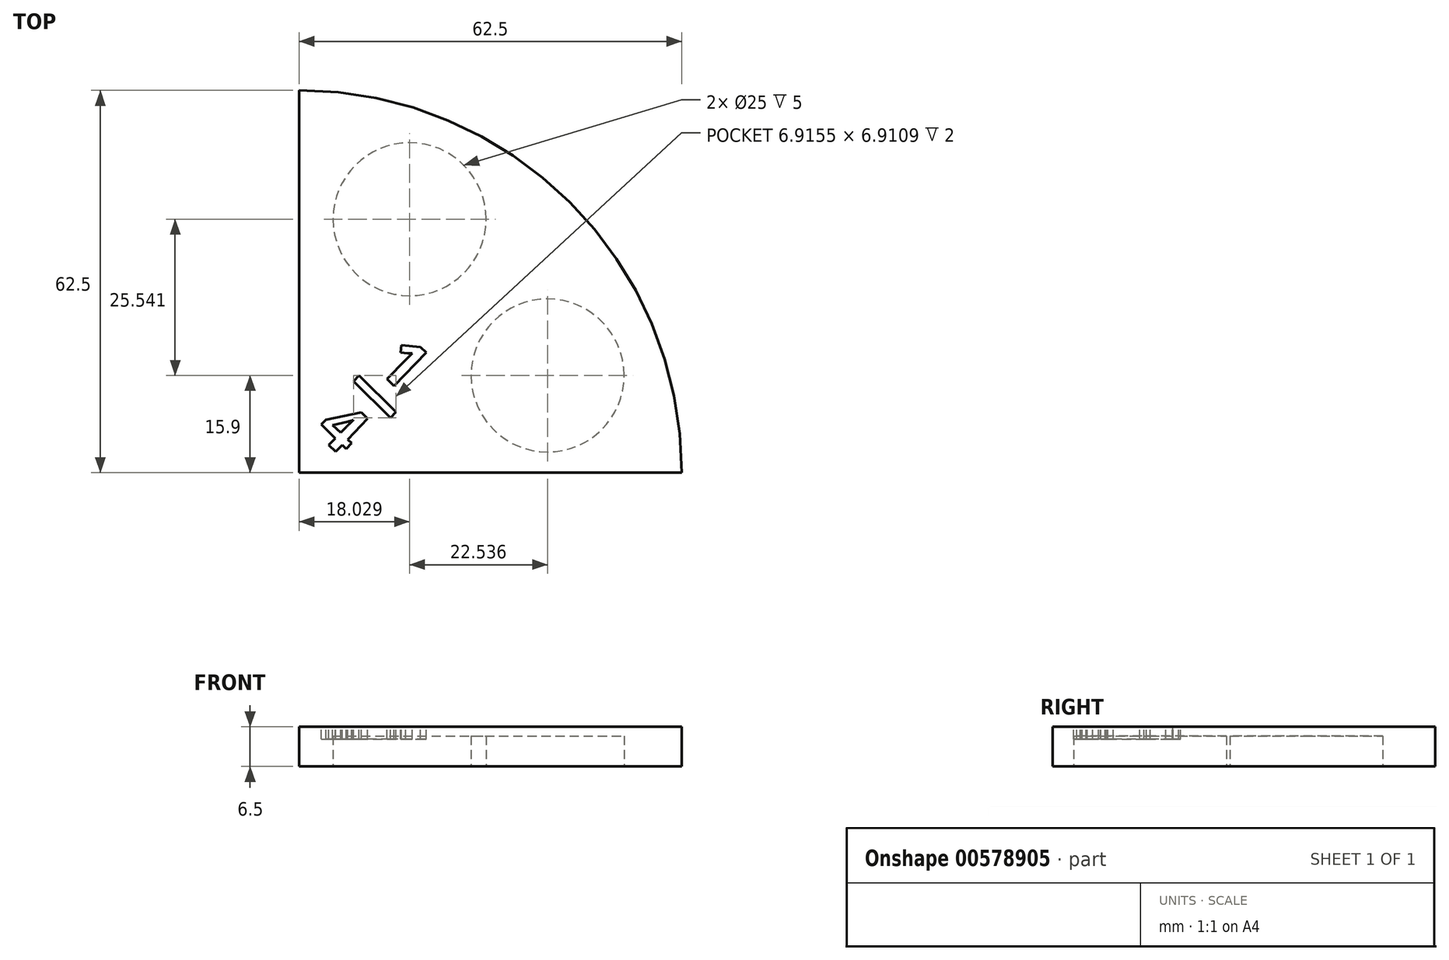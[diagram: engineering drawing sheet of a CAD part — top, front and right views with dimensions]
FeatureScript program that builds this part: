
annotation { "Feature Type Name" : "Feature", "Feature Type Description" : "" }
export const myFeature = defineFeature(function(context is Context, id is Id, definition is map)
    precondition{}
    {
        {
            var Q0;
            Q0=qCreatedBy(makeId("Top.planeOp"),FACE);
            var sketch = newSketch(context, id + "F0", { "sketchPlane" : qUnion([Q0])});
            skArc(sketch, "E0", {"start": v(62.5, 0) * mm, "mid": v(44.2, 44.2) * mm, "end": v(0, 62.5) * mm});
            skLineSegment(sketch, "E1", {"start": v(0, 62.5) * mm, "end": v(0, 0) * mm});
            skLineSegment(sketch, "E2", {"start": v(62.5, 0) * mm, "end": v(0, 0) * mm});
            skSolve(sketch);
        }
        {
            var Q0;
            Q0=makeQuery(id+"F0.imprint","IMPRINT",FACE,{"disambiguationData":[TD([[makeQuery(id+"F0.imprint","IMPRINT",EDGE,{"derivedFrom":sQuery(id+"F0.wireOp",EDGE,"E0")}),1.0]])]});
            extrude(context, id + "F1", {"entities" : qUnion([Q0]), "depth" : 6.5 * mm, "offsetDistance" : 25 * mm});
        }
        {
            var Q0;
            Q0=makeQuery(id+"F1.opExtrude","CAP_FACE",FACE,{"disambiguationData":[OSD([sQuery(id+"F0.wireOp",EDGE,"E0"),sQuery(id+"F0.wireOp",EDGE,"E1"),sQuery(id+"F0.wireOp",EDGE,"E2")])],"isStart":true});
            var sketch = newSketch(context, id + "F2", { "sketchPlane" : qUnion([Q0])});
            skCircle(sketch, "E3", {"center": v(40.56, -15.9) * mm, "radius": 12.5 * mm});
            skCircle(sketch, "E4", {"center": v(18.03, -41.44) * mm, "radius": 12.5 * mm});
            skSolve(sketch);
        }
        {
            var Q0;
            Q0=makeQuery(id+"F2.imprint","IMPRINT",FACE,{"disambiguationData":[TD([[makeQuery(id+"F2.imprint","IMPRINT",EDGE,{"derivedFrom":sQuery(id+"F2.wireOp",EDGE,"E4")}),1.0]])]});
            var Q1;
            Q1=makeQuery(id+"F2.imprint","IMPRINT",FACE,{"disambiguationData":[TD([[makeQuery(id+"F2.imprint","IMPRINT",EDGE,{"derivedFrom":sQuery(id+"F2.wireOp",EDGE,"E3")}),1.0]])]});
            extrude(context, id + "F3", {"entities" : qUnion([Q0, Q1]), "operationType" : NewBodyOperationType.REMOVE, "oppositeDirection" : true, "depth" : 5 * mm, "offsetDistance" : 25 * mm});
        }
        {
            var Q0;
            Q0=makeQuery(id+"F1.opExtrude","CAP_FACE",FACE,{"disambiguationData":[OSD([sQuery(id+"F0.wireOp",EDGE,"E0"),sQuery(id+"F0.wireOp",EDGE,"E1"),sQuery(id+"F0.wireOp",EDGE,"E2")])],"isStart":false});
            var sketch = newSketch(context, id + "F4", { "sketchPlane" : qUnion([Q0])});
            skText(sketch, "E5", { "text": "1\n4", "fontName": "OpenSans-Bold.ttf"});
            const initialGuessF4  = {"E5": [0.01236, 0.01725, 0.72039, -0.69357, 0.00762]};
            skSetInitialGuess(sketch, initialGuessF4);
            skSolve(sketch);
        }
        {
            var Q0;
            Q0 = qSketchRegion(id + "F4", true);
            extrude(context, id + "F5", {"entities" : qUnion([Q0]), "operationType" : NewBodyOperationType.REMOVE, "oppositeDirection" : true, "depth" : 2 * mm, "offsetDistance" : 25 * mm});
        }
        {
            var Q0;
            Q0=makeQuery(id+"F4.imprint","IMPRINT",FACE,{"disambiguationData":[TD([[makeQuery(id+"F4.imprint","IMPRINT",EDGE,{"derivedFrom":sQuery(id+"F4.wireOp",EDGE,"E5.sketch_text.stroke-0")}),1.0]])]});
            var sketch = newSketch(context, id + "F6", { "sketchPlane" : qUnion([Q0])});
            skLineSegment(sketch, "E6", {"start": v(9.76, 15.9) * mm, "end": v(15.82, 9.91) * mm});
            skLineSegment(sketch, "E7", {"start": v(15.82, 9.91) * mm, "end": v(14.92, 9) * mm});
            skLineSegment(sketch, "E8", {"start": v(14.92, 9) * mm, "end": v(8.9, 14.94) * mm});
            skLineSegment(sketch, "E9", {"start": v(8.9, 14.94) * mm, "end": v(9.76, 15.9) * mm});
            skSolve(sketch);
        }
        {
            var Q0;
            Q0 = qSketchRegion(id + "F6", true);
            extrude(context, id + "F7", {"entities" : qUnion([Q0]), "operationType" : NewBodyOperationType.REMOVE, "oppositeDirection" : true, "depth" : 2 * mm, "offsetDistance" : 25 * mm});
        }
    });
